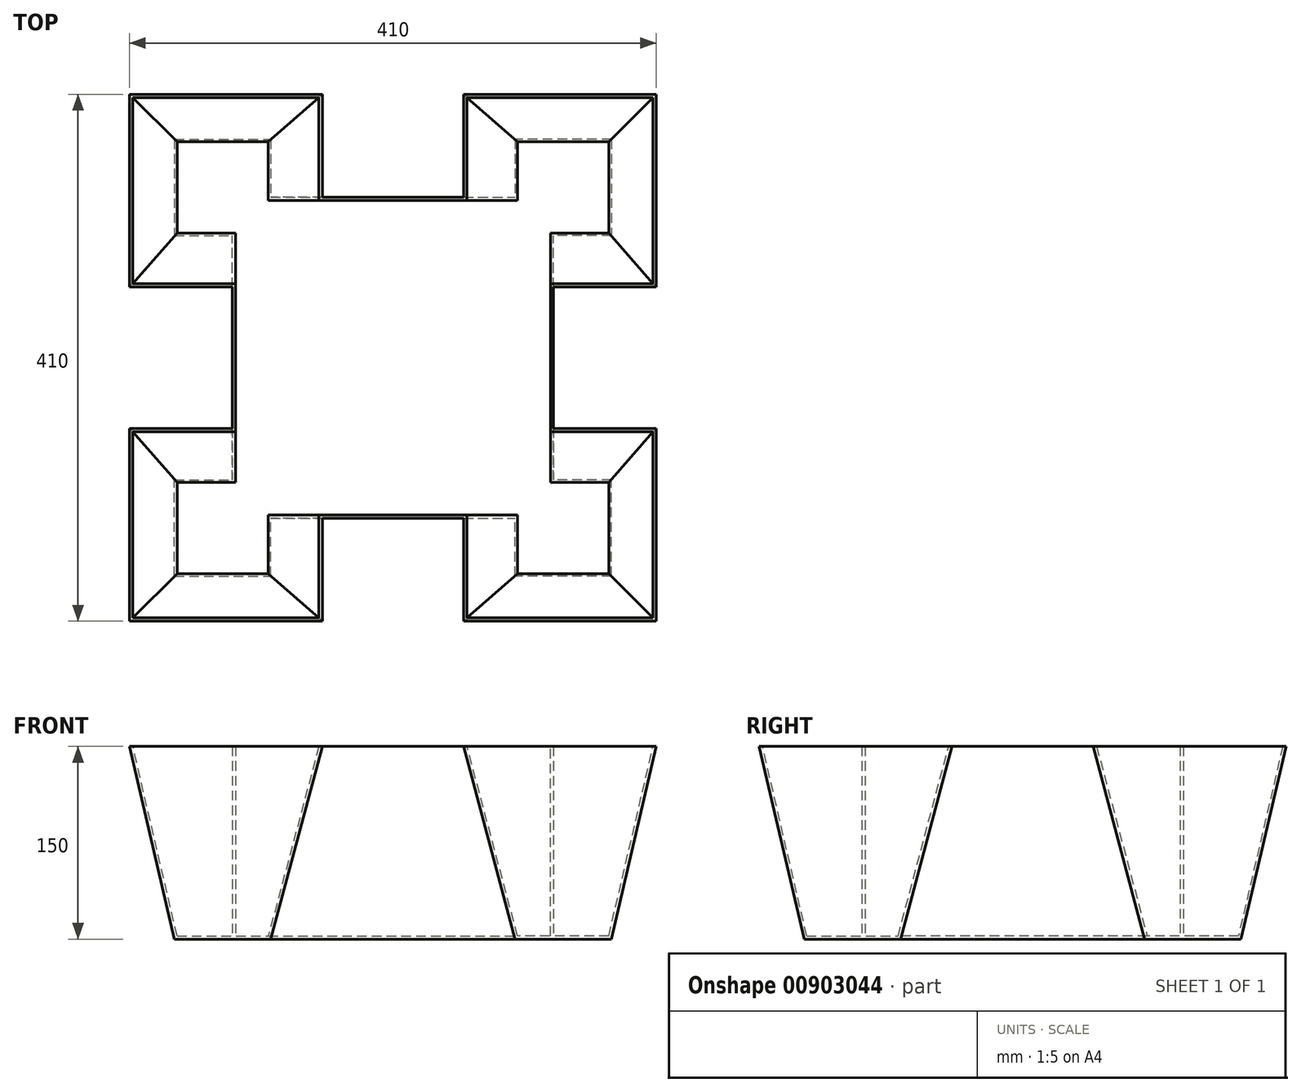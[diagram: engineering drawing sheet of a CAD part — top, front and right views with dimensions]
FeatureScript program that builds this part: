
annotation { "Feature Type Name" : "Feature", "Feature Type Description" : "" }
export const myFeature = defineFeature(function(context is Context, id is Id, definition is map)
    precondition{}
    {
        {
            var Q0;
            Q0=qCreatedBy(makeId("Top.planeOp"),FACE);
            var sketch = newSketch(context, id + "F0", { "sketchPlane" : qUnion([Q0])});
            skLineSegment(sketch, "E0.bottom", {"start": v(-55, 125) * mm, "end": v(55, 125) * mm});
            skLineSegment(sketch, "E0.top", {"start": v(-55, -125) * mm, "end": v(55, -125) * mm});
            skLineSegment(sketch, "E0.left", {"start": v(-125, 55) * mm, "end": v(-125, -55) * mm});
            skLineSegment(sketch, "E0.right", {"start": v(125, 55) * mm, "end": v(125, -55) * mm});
            skPoint(sketch, "E1", {"position": v(-130, 130) * mm});
            skLineSegment(sketch, "E2.bottom", {"start": v(-205, 205) * mm, "end": v(-55, 205) * mm});
            skLineSegment(sketch, "E2.top", {"start": v(-205, 55) * mm, "end": v(-125, 55) * mm});
            skLineSegment(sketch, "E2.left", {"start": v(-205, 205) * mm, "end": v(-205, 55) * mm});
            skLineSegment(sketch, "E2.right", {"start": v(-55, 205) * mm, "end": v(-55, 125) * mm});
            skLineSegment(sketch, "E3.1.0", {"start": v(-205, -55) * mm, "end": v(-125, -55) * mm});
            skLineSegment(sketch, "E3.1.1", {"start": v(-205, -205) * mm, "end": v(-205, -55) * mm});
            skLineSegment(sketch, "E3.1.2", {"start": v(-205, -205) * mm, "end": v(-55, -205) * mm});
            skLineSegment(sketch, "E3.1.3", {"start": v(-55, -205) * mm, "end": v(-55, -125) * mm});
            skLineSegment(sketch, "E3.2.0", {"start": v(55, -205) * mm, "end": v(55, -125) * mm});
            skLineSegment(sketch, "E3.2.1", {"start": v(205, -205) * mm, "end": v(55, -205) * mm});
            skLineSegment(sketch, "E3.2.2", {"start": v(205, -205) * mm, "end": v(205, -55) * mm});
            skLineSegment(sketch, "E3.2.3", {"start": v(205, -55) * mm, "end": v(125, -55) * mm});
            skLineSegment(sketch, "E3.3.0", {"start": v(205, 55) * mm, "end": v(125, 55) * mm});
            skLineSegment(sketch, "E3.3.1", {"start": v(205, 205) * mm, "end": v(205, 55) * mm});
            skLineSegment(sketch, "E3.3.2", {"start": v(205, 205) * mm, "end": v(55, 205) * mm});
            skLineSegment(sketch, "E3.3.3", {"start": v(55, 205) * mm, "end": v(55, 125) * mm});
            skPoint(sketch, "E3.center", {"position": v(0, 0) * mm});
            skPoint(sketch, "E4.orphan", {"position": v(-55, 55) * mm});
            skPoint(sketch, "E5.orphan", {"position": v(55, 55) * mm});
            skPoint(sketch, "E6.orphan", {"position": v(55, -55) * mm});
            skPoint(sketch, "E7.orphan", {"position": v(-55, -55) * mm});
            skSolve(sketch);
        }
        {
            var Q0;
            Q0=qCreatedBy(makeId("Top.planeOp"),FACE);
            cPlane(context, id + "F1", {"entities" : qUnion([Q0]), "cplaneType" : CPlaneType.OFFSET, "offset" : 150 * mm, "oppositeDirection" : true, "width" : 150 * mm, "height" : 150 * mm});
        }
        {
            var Q0;
            Q0=qCreatedBy(id+"F1.planeOp",FACE);
            var sketch = newSketch(context, id + "F2", { "sketchPlane" : qUnion([Q0])});
            skLineSegment(sketch, "E8.bottom", {"start": v(-95, -125) * mm, "end": v(95, -125) * mm});
            skLineSegment(sketch, "E8.top", {"start": v(-95, 125) * mm, "end": v(95, 125) * mm});
            skLineSegment(sketch, "E8.left", {"start": v(-125, -95) * mm, "end": v(-125, 95) * mm});
            skLineSegment(sketch, "E8.right", {"start": v(125, -95) * mm, "end": v(125, 95) * mm});
            skLineSegment(sketch, "E9.bottom", {"start": v(-170, 170) * mm, "end": v(-95, 170) * mm});
            skLineSegment(sketch, "E9.top", {"start": v(-170, 95) * mm, "end": v(-125, 95) * mm});
            skLineSegment(sketch, "E9.left", {"start": v(-170, 170) * mm, "end": v(-170, 95) * mm});
            skLineSegment(sketch, "E9.right", {"start": v(-95, 170) * mm, "end": v(-95, 125) * mm});
            skLineSegment(sketch, "E10.1.0", {"start": v(-170, -95) * mm, "end": v(-125, -95) * mm});
            skLineSegment(sketch, "E10.1.1", {"start": v(-95, -170) * mm, "end": v(-95, -125) * mm});
            skLineSegment(sketch, "E10.1.2", {"start": v(-170, -170) * mm, "end": v(-95, -170) * mm});
            skLineSegment(sketch, "E10.1.3", {"start": v(-170, -170) * mm, "end": v(-170, -95) * mm});
            skLineSegment(sketch, "E10.2.0", {"start": v(95, -170) * mm, "end": v(95, -125) * mm});
            skLineSegment(sketch, "E10.2.1", {"start": v(170, -95) * mm, "end": v(125, -95) * mm});
            skLineSegment(sketch, "E10.2.2", {"start": v(170, -170) * mm, "end": v(170, -95) * mm});
            skLineSegment(sketch, "E10.2.3", {"start": v(170, -170) * mm, "end": v(95, -170) * mm});
            skLineSegment(sketch, "E10.3.0", {"start": v(170, 95) * mm, "end": v(125, 95) * mm});
            skLineSegment(sketch, "E10.3.1", {"start": v(95, 170) * mm, "end": v(95, 125) * mm});
            skLineSegment(sketch, "E10.3.2", {"start": v(170, 170) * mm, "end": v(95, 170) * mm});
            skLineSegment(sketch, "E10.3.3", {"start": v(170, 170) * mm, "end": v(170, 95) * mm});
            skPoint(sketch, "E10.center", {"position": v(0, 0) * mm});
            skPoint(sketch, "E11.orphan", {"position": v(-95, 95) * mm});
            skPoint(sketch, "E12.orphan", {"position": v(95, 95) * mm});
            skPoint(sketch, "E13.orphan", {"position": v(95, -95) * mm});
            skPoint(sketch, "E14.orphan", {"position": v(-95, -95) * mm});
            skSolve(sketch);
        }
        {
            var Q0;
            Q0=makeQuery(id+"F0.imprint","IMPRINT",FACE,{"disambiguationData":[TD([[makeQuery(id+"F0.imprint","IMPRINT",EDGE,{"derivedFrom":sQuery(id+"F0.wireOp",EDGE,"E0.bottom")}),-1.0]])]});
            var Q1;
            Q1=makeQuery(id+"F2.imprint","IMPRINT",FACE,{"disambiguationData":[TD([[makeQuery(id+"F2.imprint","IMPRINT",EDGE,{"derivedFrom":sQuery(id+"F2.wireOp",EDGE,"E8.bottom")}),1.0]])]});
            loft(context, id + "F3", {"sheetProfilesArray" : [{ "sheetProfileEntities" : qUnion([Q0]) }, { "sheetProfileEntities" : qUnion([Q1]) }]});
        }
        {
            var Q0;
            Q0=makeQuery(id+"F3.opLoft","CAP_FACE",FACE,{"disambiguationData":[OSD([makeQuery(id+"F0.imprint","IMPRINT",FACE,{"disambiguationData":[TD([[makeQuery(id+"F0.imprint","IMPRINT",EDGE,{"derivedFrom":sQuery(id+"F0.wireOp",EDGE,"E0.bottom")}),-1.0]])]})])],"isStart":true});
            shell(context, id + "F4", {"entities" : qUnion([Q0]), "thickness" : 2.5 * mm});
        }
    });
